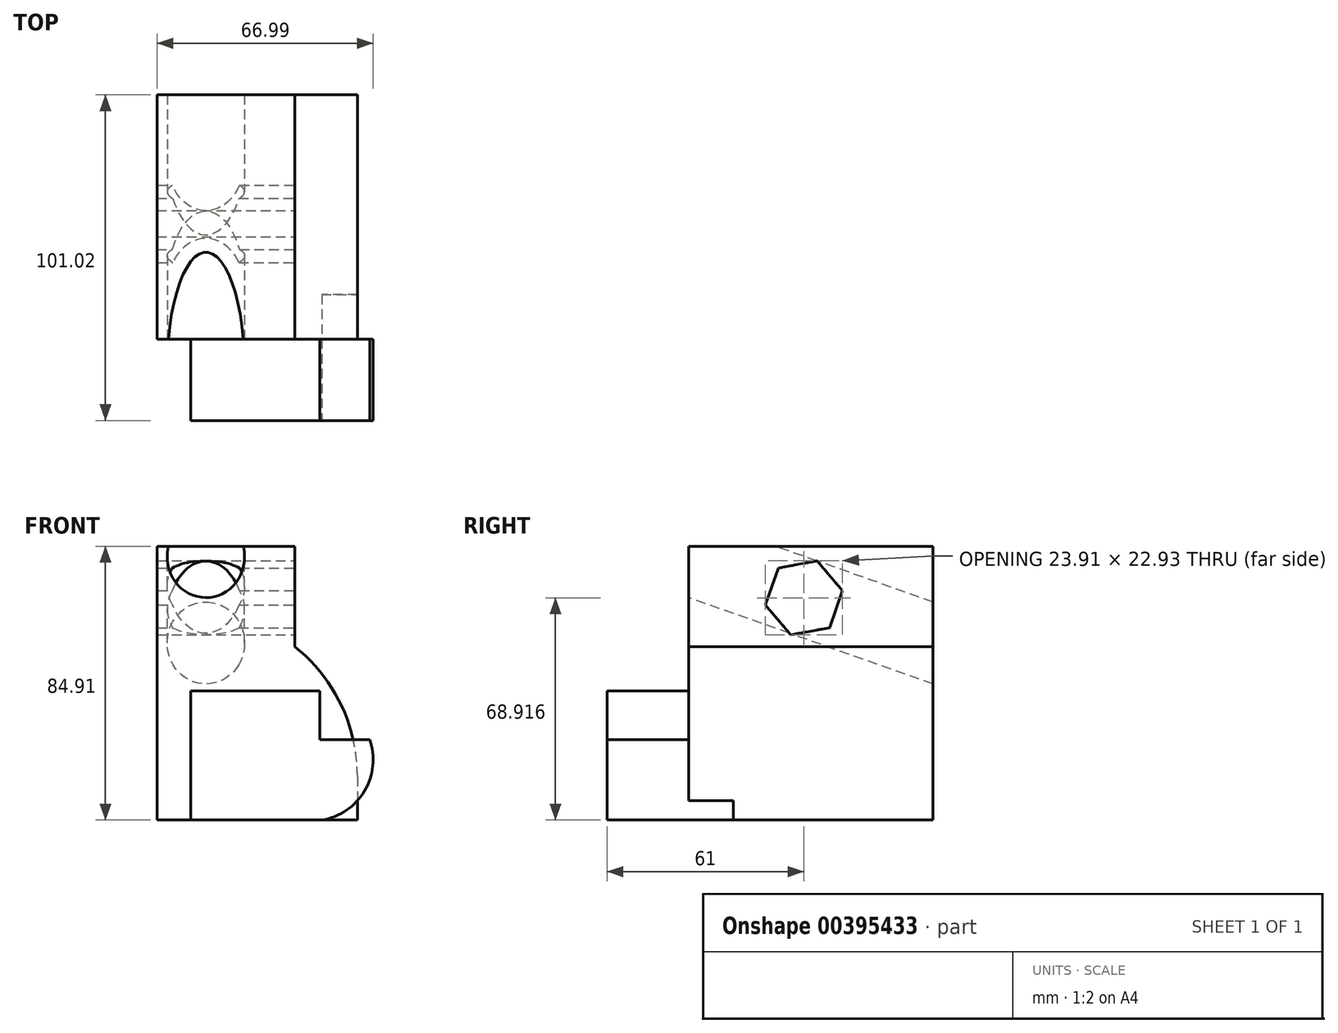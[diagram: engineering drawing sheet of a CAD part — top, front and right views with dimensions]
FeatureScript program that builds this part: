
annotation { "Feature Type Name" : "Feature", "Feature Type Description" : "" }
export const myFeature = defineFeature(function(context is Context, id is Id, definition is map)
    precondition{}
    {
        {
            var Q0;
            Q0=qCreatedBy(makeId("Top.planeOp"),FACE);
            var sketch = newSketch(context, id + "F0", { "sketchPlane" : qUnion([Q0])});
            skLineSegment(sketch, "E0.bottom", {"start": v(-27.57, 40.02) * mm, "end": v(34.5, 40.02) * mm});
            skLineSegment(sketch, "E0.top", {"start": v(-27.57, -35.73) * mm, "end": v(34.5, -35.73) * mm});
            skLineSegment(sketch, "E0.left", {"start": v(-27.57, 40.02) * mm, "end": v(-27.57, -35.73) * mm});
            skLineSegment(sketch, "E0.right", {"start": v(34.5, 40.02) * mm, "end": v(34.5, -35.73) * mm});
            skSolve(sketch);
        }
        {
            var Q0;
            Q0=makeQuery(id+"F0.imprint","IMPRINT",FACE,{"disambiguationData":[TD([[makeQuery(id+"F0.imprint","IMPRINT",EDGE,{"derivedFrom":sQuery(id+"F0.wireOp",EDGE,"E0.bottom")}),-1.0]])]});
            extrude(context, id + "F1", {"entities" : qUnion([Q0]), "depth" : 53.8 * mm});
        }
        {
            var Q0;
            Q0=makeQuery(id+"F1.opExtrude","CAP_FACE",FACE,{"disambiguationData":[OSD([sQuery(id+"F0.wireOp",EDGE,"E0.bottom"),sQuery(id+"F0.wireOp",EDGE,"E0.top"),sQuery(id+"F0.wireOp",EDGE,"E0.left"),sQuery(id+"F0.wireOp",EDGE,"E0.right")])],"isStart":false});
            var sketch = newSketch(context, id + "F2", { "sketchPlane" : qUnion([Q0])});
            skLineSegment(sketch, "E1", {"start": v(15.14, -35.73) * mm, "end": v(15.14, 40.02) * mm});
            skLineSegment(sketch, "E2", {"start": v(15.14, 40.02) * mm, "end": v(-27.57, 40.02) * mm});
            skLineSegment(sketch, "E3", {"start": v(-27.57, 40.02) * mm, "end": v(-27.57, -35.73) * mm});
            skLineSegment(sketch, "E4", {"start": v(-27.57, -35.73) * mm, "end": v(15.14, -35.73) * mm});
            skSolve(sketch);
        }
        {
            var Q0;
            Q0=makeQuery(id+"F2.imprint","IMPRINT",FACE,{"disambiguationData":[TD([[makeQuery(id+"F2.imprint","IMPRINT",EDGE,{"derivedFrom":sQuery(id+"F2.wireOp",EDGE,"E1")}),1.0]])]});
            extrude(context, id + "F3", {"entities" : qUnion([Q0]), "operationType" : NewBodyOperationType.ADD, "depth" : 31.1 * mm, "offsetDistance" : 25 * mm});
        }
        {
            var Q0;
            Q0=makeQuery(id+"F3.opExtrude","SWEPT_FACE",FACE,{"disambiguationData":[OSD([sQuery(id+"F2.wireOp",EDGE,"E1")])]});
            var sketch = newSketch(context, id + "F4", { "sketchPlane" : qUnion([Q0])});
            skCircle(sketch, "E5.cCircle", {"center": v(0, 68.92) * mm, "radius": 12.16 * mm, "construction": true});
            skLineSegment(sketch, "E5.0", {"start": v(11.96, 71.14) * mm, "end": v(7.9, 59.67) * mm});
            skLineSegment(sketch, "E5.1", {"start": v(7.9, 59.67) * mm, "end": v(-4.05, 57.45) * mm});
            skLineSegment(sketch, "E5.2", {"start": v(-4.05, 57.45) * mm, "end": v(-11.96, 66.7) * mm});
            skLineSegment(sketch, "E5.3", {"start": v(-11.96, 66.7) * mm, "end": v(-7.9, 78.16) * mm});
            skLineSegment(sketch, "E5.4", {"start": v(-7.9, 78.16) * mm, "end": v(4.05, 80.38) * mm});
            skLineSegment(sketch, "E5.5", {"start": v(4.05, 80.38) * mm, "end": v(11.96, 71.14) * mm});
            skSolve(sketch);
        }
        {
            var Q0;
            Q0 = qSketchRegion(id + "F4", true);
            extrude(context, id + "F5", {"entities" : qUnion([Q0]), "operationType" : NewBodyOperationType.REMOVE, "oppositeDirection" : true, "depth" : 50.48 * mm, "offsetDistance" : 25 * mm});
        }
        {
            var Q0;
            Q0=makeQuery(id+"F5.boolean.opBoolean","COPY",FACE,{"derivedFrom":makeQuery(id+"F5.opExtrude","SWEPT_FACE",FACE,{"disambiguationData":[OSD([sQuery(id+"F4.wireOp",EDGE,"E5.0")])]})});
            var sketch = newSketch(context, id + "F6", { "sketchPlane" : qUnion([Q0])});
            skCircle(sketch, "E6", {"center": v(-12.43, 65.12) * mm, "radius": 12 * mm});
            skSolve(sketch);
        }
        {
            var Q0;
            Q0 = qSketchRegion(id + "F6", true);
            extrude(context, id + "F7", {"entities" : qUnion([Q0]), "operationType" : NewBodyOperationType.REMOVE, "oppositeDirection" : true, "depth" : 57.15 * mm, "offsetDistance" : 25 * mm, "hasSecondDirection" : true, "secondDirectionOppositeDirection" : false, "secondDirectionDepth" : 70.53 * mm});
        }
        {
            var Q0;
            Q0=makeQuery(id+"F3.boolean.opBoolean","MERGE",FACE,{"derivedFrom":[makeQuery(id+"F1.opExtrude","SWEPT_FACE",FACE,{"disambiguationData":[OSD([sQuery(id+"F0.wireOp",EDGE,"E0.top")])]}),makeQuery(id+"F3.opExtrude","SWEPT_FACE",FACE,{"disambiguationData":[OSD([sQuery(id+"F2.wireOp",EDGE,"E4")])]})]});
            var sketch = newSketch(context, id + "F8", { "sketchPlane" : qUnion([Q0])});
            skLineSegment(sketch, "E7", {"start": v(-17.13, 0) * mm, "end": v(-17.13, 40) * mm});
            skLineSegment(sketch, "E8", {"start": v(-17.13, 40) * mm, "end": v(22.87, 40) * mm});
            skLineSegment(sketch, "E9", {"start": v(22.87, 40) * mm, "end": v(22.87, 25) * mm});
            skLineSegment(sketch, "E10", {"start": v(22.87, 25) * mm, "end": v(57.87, 25) * mm});
            skLineSegment(sketch, "E11", {"start": v(57.87, 25) * mm, "end": v(57.87, 0) * mm});
            skLineSegment(sketch, "E12", {"start": v(57.87, 0) * mm, "end": v(-17.13, 0) * mm});
            skSolve(sketch);
        }
        {
            var Q0;
            {var subQ0=sQuery(id+"F8.wireOp",EDGE,"E11");Q0=makeQuery(id+"F8.imprint","IMPRINT",FACE,{"disambiguationData":[TD([[makeQuery(id+"F8.imprint","IMPRINT",EDGE,{"derivedFrom":subQ0}),-1.0]])]});}
            var Q1;
            {var subQ5=sQuery(id+"F8.wireOp",EDGE,"E7");Q1=makeQuery(id+"F8.imprint","IMPRINT",FACE,{"disambiguationData":[TD([[makeQuery(id+"F8.imprint","IMPRINT",EDGE,{"derivedFrom":subQ5}),-1.0]])]});}
            extrude(context, id + "F9", {"entities" : qUnion([Q0, Q1]), "operationType" : NewBodyOperationType.ADD, "depth" : 25.27 * mm, "offsetDistance" : 25 * mm});
        }
        {
            var Q0;
            Q0=makeQuery(id+"F9.opExtrude","CAP_FACE",FACE,{"disambiguationData":[OSD([sQuery(id+"F8.wireOp",EDGE,"E7"),sQuery(id+"F8.wireOp",EDGE,"E8"),sQuery(id+"F8.wireOp",EDGE,"E9"),sQuery(id+"F8.wireOp",EDGE,"E10"),sQuery(id+"F8.wireOp",EDGE,"E11"),sQuery(id+"F8.wireOp",EDGE,"E12")])],"isStart":false});
            var sketch = newSketch(context, id + "F10", { "sketchPlane" : qUnion([Q0])});
            skCircle(sketch, "E13", {"center": v(20.42, 18.75) * mm, "radius": 19 * mm});
            skSolve(sketch);
        }
        {
            var Q0;
            {var subQ5=makeQuery(id+"F9.opExtrude","CAP_EDGE",EDGE,{"disambiguationData":[OSD([sQuery(id+"F8.wireOp",EDGE,"E11")])],"isStart":false});Q0=makeQuery(id+"F10.imprint","IMPRINT",FACE,{"disambiguationData":[TD([[makeQuery(id+"F10.imprint","IMPRINT",EDGE,{"derivedFrom":subQ5}),-1.0]])]});}
            extrude(context, id + "F11", {"entities" : qUnion([Q0]), "operationType" : NewBodyOperationType.REMOVE, "oppositeDirection" : true, "depth" : 39.06 * mm, "offsetDistance" : 25 * mm});
        }
        {
            var Q0;
            Q0=makeQuery(id+"F1.opExtrude","CAP_EDGE",EDGE,{"disambiguationData":[OSD([sQuery(id+"F0.wireOp",EDGE,"E0.right")])],"isStart":false});
            fillet(context, id + "F12", {"entities" : qUnion([Q0]), "tangentPropagation" : true, "radius" : 51.6 * mm, "defaultsChanged" : true, "vertexSettings" : [], "allowEdgeOverflow" : false});
        }
    });
